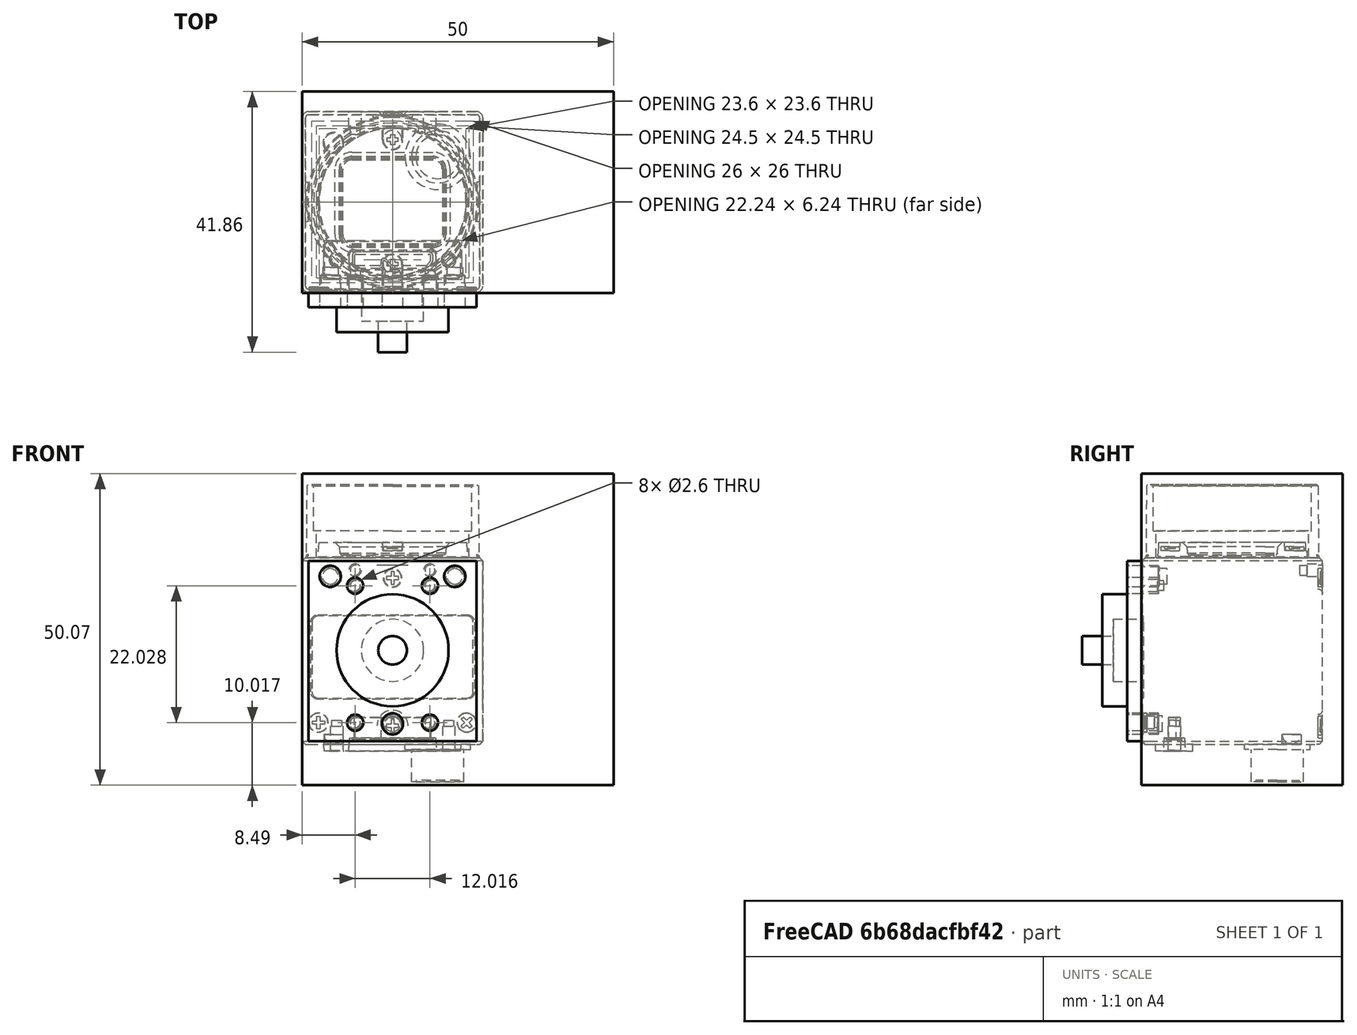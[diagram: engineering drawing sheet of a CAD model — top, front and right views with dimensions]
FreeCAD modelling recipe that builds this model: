
FCSTD DOCUMENT  (FreeCAD 0.15R4671 (Git))
Label: Flir_BlackflyS_ThorLabs_post_mount
License: All rights reserved
LicenseURL: http://en.wikipedia.org/wiki/All_rights_reserved
objects: Sketcher::SketchObject×6, PartDesign::Pocket×4, Part::Feature×2, PartDesign::Pad×2, Mesh::Feature×1
note: 20 computed .brp shape members not serialized (recipe doc carries the construction recipe); baked Part::Feature solids carry a one-line shape summary decoded from their .brp

FEATURE [Part::Feature] Part__Feature  label="FL2-020-R0"
  shape: bbox 29.97 x 29 x 47.76 mm, 421 faces (baked)
FEATURE [Sketcher::SketchObject] Sketch
  Placement = pos=(0,-14.5,0) rot=(1,0,0;1.5708rad)
  Support = -> Part__Feature [Face75]
  sketch-geometry (4):
    g0: LineSegment StartX=-13.5 StartY=12.3818 StartZ=0 EndX=13.5 EndY=12.3818 EndZ=0
    g1: LineSegment StartX=13.5 StartY=12.3818 StartZ=0 EndX=13.5 EndY=-16.6182 EndZ=0
    g2: LineSegment StartX=13.5 StartY=-16.6182 StartZ=0 EndX=-13.5 EndY=-16.6182 EndZ=0
    g3: LineSegment StartX=-13.5 StartY=-16.6182 StartZ=0 EndX=-13.5 EndY=12.3818 EndZ=0
  constraints (14):
    c: Coincident(g0,g1)
    c: Coincident(g1,g2)
    c: Coincident(g2,g3)
    c: Coincident(g3,g0)
    c: Horizontal(g0)
    c: Horizontal(g2)
    c: Vertical(g1)
    c: Vertical(g3)
    c: Distance(g0) = 27
    c: Distance(g3) = 29
    c: Equal(g1,g3)
    c: Equal(g0,g2)
    c: DistanceX(g0) = -13.5
    c: DistanceY(g0) = 12.3818
FEATURE [PartDesign::Pad] Pad
  Length = 2.4
  Length2 = 100
  Sketch = -> Sketch
  Type = 0
FEATURE [Sketcher::SketchObject] Sketch001
  Placement = pos=(0,-16.9,0) rot=(1,0,0;1.5708rad)
  Support = -> Pad [Face143]
  sketch-geometry (7):
    g0: Circle CenterX=-10.006 CenterY=9.88074 CenterZ=0 NormalX=0 NormalY=0 NormalZ=1 Radius=1.7
    g1: Circle CenterX=9.99406 CenterY=9.87655 CenterZ=0 NormalX=0 NormalY=0 NormalZ=1 Radius=1.7
    g2: Circle CenterX=-0.007411 CenterY=-13.8147 CenterZ=0 NormalX=0 NormalY=0 NormalZ=1 Radius=1.7
    g3: Circle CenterX=-5.99587 CenterY=-13.6429 CenterZ=0 NormalX=0 NormalY=0 NormalZ=1 Radius=1.3
    g4: Circle CenterX=6.00612 CenterY=-13.6271 CenterZ=0 NormalX=0 NormalY=0 NormalZ=1 Radius=1.3
    g5: Circle CenterX=6.00293 CenterY=8.3827 CenterZ=0 NormalX=0 NormalY=0 NormalZ=1 Radius=1.3
    g6: Circle CenterX=-6.00964 CenterY=8.38521 CenterZ=0 NormalX=0 NormalY=0 NormalZ=1 Radius=1.3
  constraints (21):
    c: Radius(g0) = 1.7
    c: Radius(g1) = 1.7
    c: Radius(g2) = 1.7
    c: Radius(g3) = 1.3
    c: Radius(g4) = 1.3
    c: Radius(g5) = 1.3
    c: Radius(g6) = 1.3
    c: DistanceX(g0) = -10.006
    c: DistanceY(g0) = 9.88074
    c: DistanceX(g6) = -6.00964
    c: DistanceY(g6) = 8.38521
    c: DistanceX(g5) = 6.00293
    c: DistanceY(g5) = 8.3827
    c: DistanceX(g1) = 9.99406
    c: DistanceY(g1) = 9.87655
    c: DistanceX(g4) = 6.00612
    c: DistanceY(g4) = -13.6271
    c: DistanceX(g2) = -0.007411
    c: DistanceY(g2) = -13.8147
    c: DistanceX(g3) = -5.99587
    c: DistanceY(g3) = -13.6429
FEATURE [PartDesign::Pocket] Pocket
  Length = 5
  Sketch = -> Sketch001
  Type = 0
FEATURE [Sketcher::SketchObject] Sketch002
  Placement = pos=(-14.5,0,0) rot=(0.57735,-0.57735,-0.57735;2.0944rad)
  Support = -> Pocket [Face137]
  sketch-geometry (4):
    g0: LineSegment StartX=-17.7305 StartY=26.4121 StartZ=0 EndX=14.6302 EndY=26.4121 EndZ=0
    g1: LineSegment StartX=14.6302 StartY=26.4121 StartZ=0 EndX=14.6302 EndY=-23.6629 EndZ=0
    g2: LineSegment StartX=14.6302 StartY=-23.6629 StartZ=0 EndX=-17.7305 EndY=-23.6629 EndZ=0
    g3: LineSegment StartX=-17.7305 StartY=-23.6629 StartZ=0 EndX=-17.7305 EndY=26.4121 EndZ=0
  constraints (14):
    c: Coincident(g0,g1)
    c: Coincident(g1,g2)
    c: Coincident(g2,g3)
    c: Coincident(g3,g0)
    c: Horizontal(g0)
    c: Horizontal(g2)
    c: Vertical(g1)
    c: Vertical(g3)
    c: DistanceX(g0) = -17.7305
    c: DistanceY(g0) = 26.4121
    c: DistanceX(g0) = 14.6302
    c: DistanceY(g0) = 26.4121
    c: DistanceX(g1) = 14.6302
    c: DistanceY(g1) = -23.6629
FEATURE [PartDesign::Pocket] Pocket001
  Length = 50
  Sketch = -> Sketch002
  Type = 0
FEATURE [Sketcher::SketchObject] Sketch003
  Placement = pos=(0,-16.9,0) rot=(1,0,0;1.5708rad)
  Support = -> Pocket001 [Face4]
  sketch-geometry (1):
    g0: Circle CenterX=0 CenterY=-2 CenterZ=0 NormalX=0 NormalY=0 NormalZ=1 Radius=9
  constraints (3):
    c: Radius(g0) = 9
    c: DistanceY(g-1,g0) = -2
    c: DistanceX(g-1,g0) = 0
FEATURE [PartDesign::Pad] Pad001
  Length = 4
  Length2 = 100
  Sketch = -> Sketch003
  Type = 0
FEATURE [Sketcher::SketchObject] Sketch004
  Placement = pos=(0,-14.6302,0) rot=(0,0.707107,0.707107;3.14159rad)
  Support = -> Pad001 [Face2]
  sketch-geometry (1):
    g0: Circle CenterX=0 CenterY=-2 CenterZ=0 NormalX=0 NormalY=0 NormalZ=1 Radius=5
  constraints (3):
    c: DistanceX(g-1,g0) = 0
    c: DistanceY(g-1,g0) = -2
    c: Radius(g0) = 5
FEATURE [PartDesign::Pocket] Pocket002
  Length = 4.5
  Sketch = -> Sketch004
  Type = 0
FEATURE [Sketcher::SketchObject] Sketch005
  Placement = pos=(0,-19.1302,0) rot=(0,0.707107,0.707107;3.14159rad)
  Support = -> Pocket002 [Face16]
  sketch-geometry (1):
    g0: Circle CenterX=0 CenterY=-2 CenterZ=0 NormalX=0 NormalY=0 NormalZ=1 Radius=2.3
  constraints (3):
    c: DistanceX(g-1,g0) = 0
    c: DistanceY(g-1,g0) = -2
    c: Radius(g0) = 2.3
FEATURE [PartDesign::Pocket] Pocket003
  Length = 5
  Sketch = -> Sketch005
  Type = 0
FEATURE [Part::Feature] Pocket003001  label="Pocket004"
  shape: bbox 27 x 6.27 x 29 mm, 18 faces (baked)
FEATURE [Mesh::Feature] Mesh  label="Pocket003 (Meshed)"
